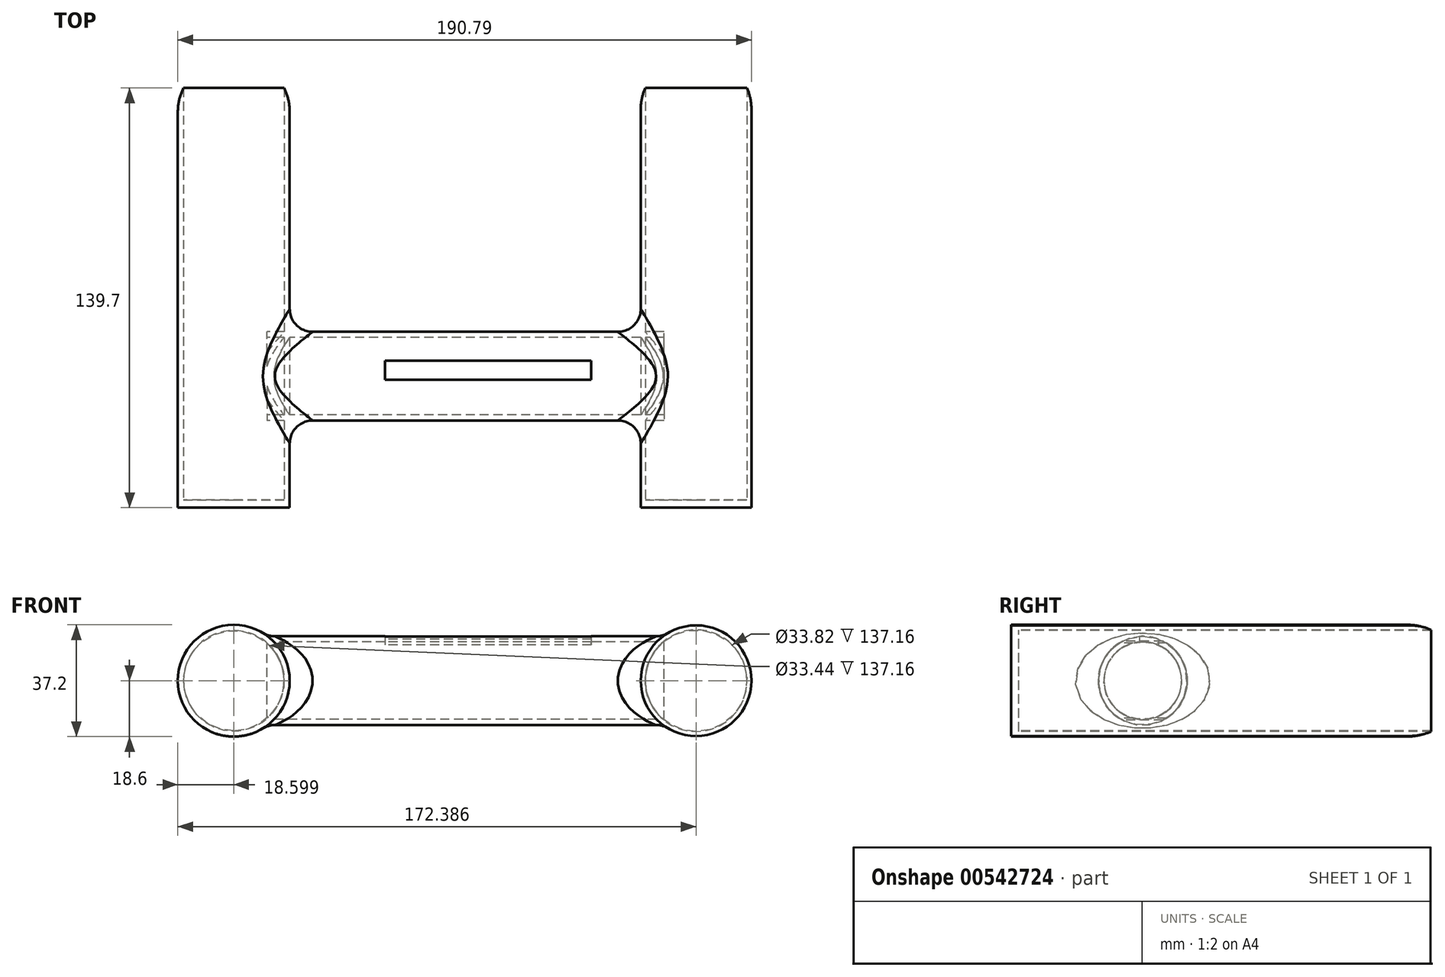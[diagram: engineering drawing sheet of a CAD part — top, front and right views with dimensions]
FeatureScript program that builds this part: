
annotation { "Feature Type Name" : "Feature", "Feature Type Description" : "" }
export const myFeature = defineFeature(function(context is Context, id is Id, definition is map)
    precondition{}
    {
        {
            var Q0;
            Q0=qCreatedBy(makeId("Right.planeOp"),FACE);
            var sketch = newSketch(context, id + "F0", { "sketchPlane" : qUnion([Q0])});
            skCircle(sketch, "E0", {"center": v(43.75, 0) * mm, "radius": 14.76 * mm});
            skCircle(sketch, "E1", {"center": v(43.75, 0) * mm, "radius": 12.92 * mm});
            skSolve(sketch);
        }
        {
            var Q0;
            Q0=makeQuery(id+"F0.imprint","IMPRINT",FACE,{"disambiguationData":[TD([[makeQuery(id+"F0.imprint","IMPRINT",EDGE,{"derivedFrom":sQuery(id+"F0.wireOp",EDGE,"E0")}),1.0]])]});
            extrude(context, id + "F1", {"entities" : qUnion([Q0]), "depth" : 132.08 * mm, "offsetDistance" : 25.4 * mm});
        }
        {
            var Q0;
            Q0=qCreatedBy(makeId("Front.planeOp"),FACE);
            var sketch = newSketch(context, id + "F2", { "sketchPlane" : qUnion([Q0])});
            skCircle(sketch, "E2", {"center": v(-11.1, 0) * mm, "radius": 18.6 * mm});
            skCircle(sketch, "E3", {"center": v(142.7, 0) * mm, "radius": 18.4 * mm});
            skCircle(sketch, "E4", {"center": v(142.7, 0) * mm, "radius": 16.91 * mm});
            skCircle(sketch, "E5", {"center": v(-11.1, 0) * mm, "radius": 16.72 * mm});
            skSolve(sketch);
        }
        {
            var Q0;
            Q0=makeQuery(id+"F2.imprint","IMPRINT",FACE,{"disambiguationData":[TD([[makeQuery(id+"F2.imprint","IMPRINT",EDGE,{"derivedFrom":sQuery(id+"F2.wireOp",EDGE,"E2")}),1.0]])]});
            var Q1;
            Q1=makeQuery(id+"F2.imprint","IMPRINT",FACE,{"disambiguationData":[TD([[makeQuery(id+"F2.imprint","IMPRINT",EDGE,{"derivedFrom":sQuery(id+"F2.wireOp",EDGE,"E3")}),1.0]])]});
            extrude(context, id + "F3", {"entities" : qUnion([Q0, Q1]), "operationType" : NewBodyOperationType.ADD, "oppositeDirection" : true, "depth" : 139.7 * mm, "offsetDistance" : 25.4 * mm});
        }
        {
            var Q0;
            Q0=qCreatedBy(makeId("Front.planeOp"),FACE);
            var sketch = newSketch(context, id + "F4", { "sketchPlane" : qUnion([Q0])});
            skCircle(sketch, "E6", {"center": v(-11.02, 0.36) * mm, "radius": 17.45 * mm});
            skCircle(sketch, "E7", {"center": v(142.47, 0.22) * mm, "radius": 17.44 * mm});
            skSolve(sketch);
        }
        {
            var Q0;
            Q0 = qSketchRegion(id + "F4", true);
            extrude(context, id + "F5", {"entities" : qUnion([Q0]), "operationType" : NewBodyOperationType.ADD, "oppositeDirection" : true, "depth" : 2.54 * mm, "offsetDistance" : 25.4 * mm});
        }
        {
            var Q0;
            Q0=qCreatedBy(makeId("Top.planeOp"),FACE);
            var sketch = newSketch(context, id + "F6", { "sketchPlane" : qUnion([Q0])});
            skLineSegment(sketch, "E8", {"start": v(107.8, 48.93) * mm, "end": v(39.22, 48.93) * mm});
            skLineSegment(sketch, "E9", {"start": v(107.8, 48.93) * mm, "end": v(107.8, 42.6) * mm});
            skLineSegment(sketch, "E10", {"start": v(107.8, 42.6) * mm, "end": v(39.22, 42.6) * mm});
            skLineSegment(sketch, "E11", {"start": v(39.22, 42.6) * mm, "end": v(39.22, 48.93) * mm});
            skSolve(sketch);
        }
        {
            var Q0;
            Q0 = qSketchRegion(id + "F6", true);
            extrude(context, id + "F7", {"entities" : qUnion([Q0]), "operationType" : NewBodyOperationType.REMOVE, "depth" : 13.72 * mm, "offsetDistance" : 25.4 * mm});
        }
        {
            var Q0;
            Q0 = qSketchRegion(id + "F6", true);
            extrude(context, id + "F8", {"entities" : qUnion([Q0]), "operationType" : NewBodyOperationType.REMOVE, "depth" : 23.88 * mm, "offsetDistance" : 25.4 * mm});
        }
        {
            var Q0;
            Q0=makeQuery(id+"F3.boolean.opBoolean","INTERSECT",EDGE,{"derivedFrom":[makeQuery(id+"F1.opExtrude","SWEPT_FACE",FACE,{"disambiguationData":[OSD([sQuery(id+"F0.wireOp",EDGE,"E0")])]}),makeQuery(id+"F3.opExtrude","SWEPT_FACE",FACE,{"disambiguationData":[OSD([sQuery(id+"F2.wireOp",EDGE,"E2")])]})]});
            fillet(context, id + "F9", {"entities" : qUnion([Q0]), "radius" : 7.62 * mm, "tangentPropagation" : true, "allowEdgeOverflow" : false});
        }
        {
            var Q0;
            Q0=makeQuery(id+"F3.boolean.opBoolean","INTERSECT",EDGE,{"derivedFrom":[makeQuery(id+"F1.opExtrude","SWEPT_FACE",FACE,{"disambiguationData":[OSD([sQuery(id+"F0.wireOp",EDGE,"E0")])]}),makeQuery(id+"F3.opExtrude","SWEPT_FACE",FACE,{"disambiguationData":[OSD([sQuery(id+"F2.wireOp",EDGE,"E3")])]})]});
            fillet(context, id + "F10", {"entities" : qUnion([Q0]), "radius" : 7.62 * mm, "tangentPropagation" : true, "allowEdgeOverflow" : false});
        }
        {
            var Q0;
            Q0=makeQuery(id+"F3.opExtrude","CAP_EDGE",EDGE,{"disambiguationData":[OSD([sQuery(id+"F2.wireOp",EDGE,"E3")])],"isStart":false});
            var Q1;
            Q1=makeQuery(id+"F3.opExtrude","CAP_EDGE",EDGE,{"disambiguationData":[OSD([sQuery(id+"F2.wireOp",EDGE,"E2")])],"isStart":false});
            fillet(context, id + "F11", {"entities" : qUnion([Q0, Q1]), "radius" : 17.78 * mm, "rho" : 0.5, "crossSection" : FilletCrossSection.CONIC, "allowEdgeOverflow" : false});
        }
    });
